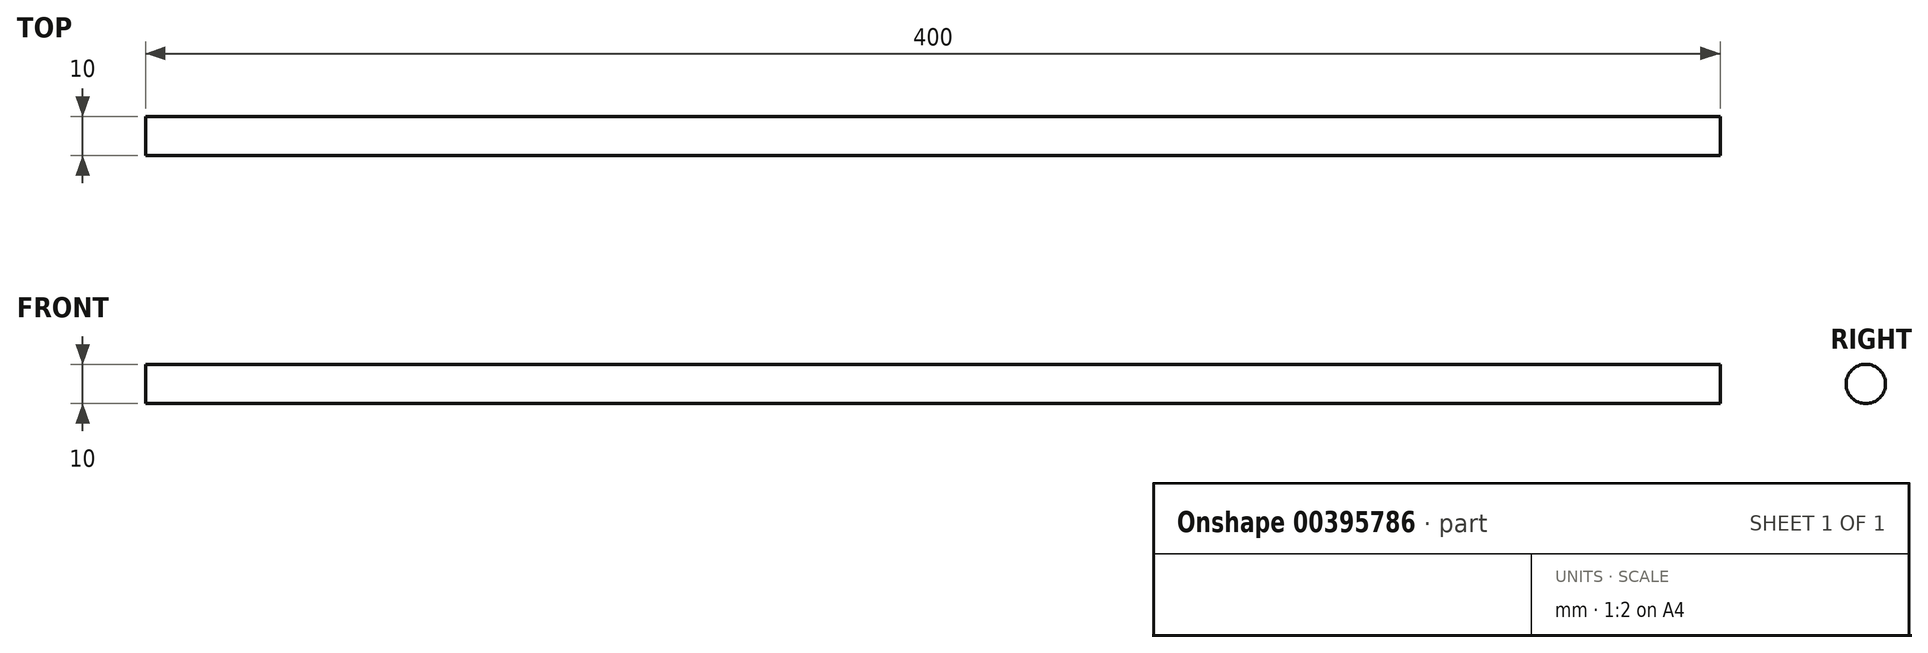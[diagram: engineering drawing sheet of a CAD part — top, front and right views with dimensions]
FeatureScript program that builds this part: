
annotation { "Feature Type Name" : "Feature", "Feature Type Description" : "" }
export const myFeature = defineFeature(function(context is Context, id is Id, definition is map)
    precondition{}
    {
        {
            var Q0;
            Q0=qCreatedBy(makeId("Front.planeOp"),FACE);
            var sketch = newSketch(context, id + "F0", { "sketchPlane" : qUnion([Q0])});
            skLineSegment(sketch, "E0.bottom", {"start": v(0, 0) * mm, "end": v(-400, 0) * mm});
            skLineSegment(sketch, "E0.top", {"start": v(0, 5) * mm, "end": v(-400, 5) * mm});
            skLineSegment(sketch, "E0.left", {"start": v(0, 0) * mm, "end": v(0, 5) * mm});
            skLineSegment(sketch, "E0.right", {"start": v(-400, 0) * mm, "end": v(-400, 5) * mm});
            skSolve(sketch);
        }
        {
            var Q0;
            Q0 = qSketchRegion(id + "F0", true);
            var Q1;
            Q1=sQuery(id+"F0.wireOp",EDGE,"E0.bottom");
            revolve(context, id + "F1", {"entities" : qUnion([Q0]), "axis" : qUnion([Q1]), "revolveType" : RevolveType.FULL});
        }
    });
